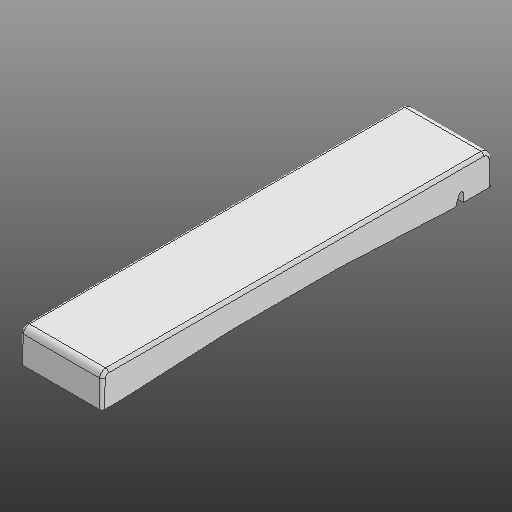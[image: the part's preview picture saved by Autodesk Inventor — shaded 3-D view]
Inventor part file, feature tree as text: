
AUTODESK INVENTOR PART (.ipt)
format: ipt  version: 2020 (Build 240168000, 168)  size: 312,832 bytes
history: native  units: in
note: dims shown in document units (in); Inventor stores cm internally (conversion verified against a paired STEP export)
features: extrude x4, other x3, fillet x2
ambient origin geometry x8: Origin, YZ Plane, XZ Plane, XY Plane, X Axis, Y Axis, Z Axis, Center Point
bodies: Solid1 (feature_tree)
feature tree (9):
  other  "Slot Start Plane"
  other  "Key Profile"
  extrude  "Upper (u)"  TaperAngle=0.0deg  [1 undecoded]
  extrude  "Lower (d)"  TaperAngle=0.0deg  [1 undecoded]
  extrude  "Protrusion Cutout"  Depth=0.0591in
  fillet  "Front Fillet"  Radius=0.1374in
  extrude  "Slot"  [1 undecoded]
  fillet  "Edge Softening"  Radius=0.0787in
  other  "Slot Sketch"
note: 3 required parameter values undecoded (feature->parameter linkage not recoverable at this tier; creation-order binding heuristic only, values carry confidence <= 0.55)
